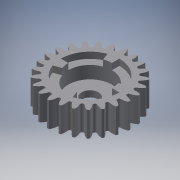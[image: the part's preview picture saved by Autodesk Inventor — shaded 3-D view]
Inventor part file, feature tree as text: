
AUTODESK INVENTOR PART (.ipt)
format: ipt  version: 2017 (Build 210142000, 142)  size: 281,600 bytes
history: native  units: mm
features: extrude x5, sketch x4, pattern_circular x2
ambient origin geometry x8: Origin, YZ Plane, XZ Plane, XY Plane, X Axis, Y Axis, Z Axis, Center Point
bodies: Solid1 (feature_tree)
feature tree (11):
  sketch  "Sketch1"  dims[d0=20.0mm d1=0.0mm]
  extrude  "Extrusion1"  TaperAngle=0.0deg  [1 undecoded]
  extrude  "Extrusion2"  Depth=10.0mm TaperAngle=360.0deg
  pattern_circular  "Circular Pattern1"  [2 undecoded]
  extrude  "Extrusion3"  Depth=15.0mm TaperAngle=0.0deg
  extrude  "Extrusion4"  Depth=5.0mm
  extrude  "Extrusion5"  Depth=5.0mm
  pattern_circular  "Circular Pattern2"  [2 undecoded]
  sketch  "Sketch2"  dims[d2=10.0mm d3=0.0mm d4=250.0mm d5=360.0deg]
  sketch  "Sketch3"  dims[d7=13.5mm]
  sketch  "Sketch4"  dims[d8=10.0mm d9=0.0mm d10=35.0mm d11=15.0mm d12=0.0mm d13=6.0mm d14=12.217305mm d15=5.0mm d16=0.0mm d17=40.0mm d18=360.0deg]
note: 5 required parameter values undecoded (feature->parameter linkage not recoverable at this tier; creation-order binding heuristic only, values carry confidence <= 0.55)
